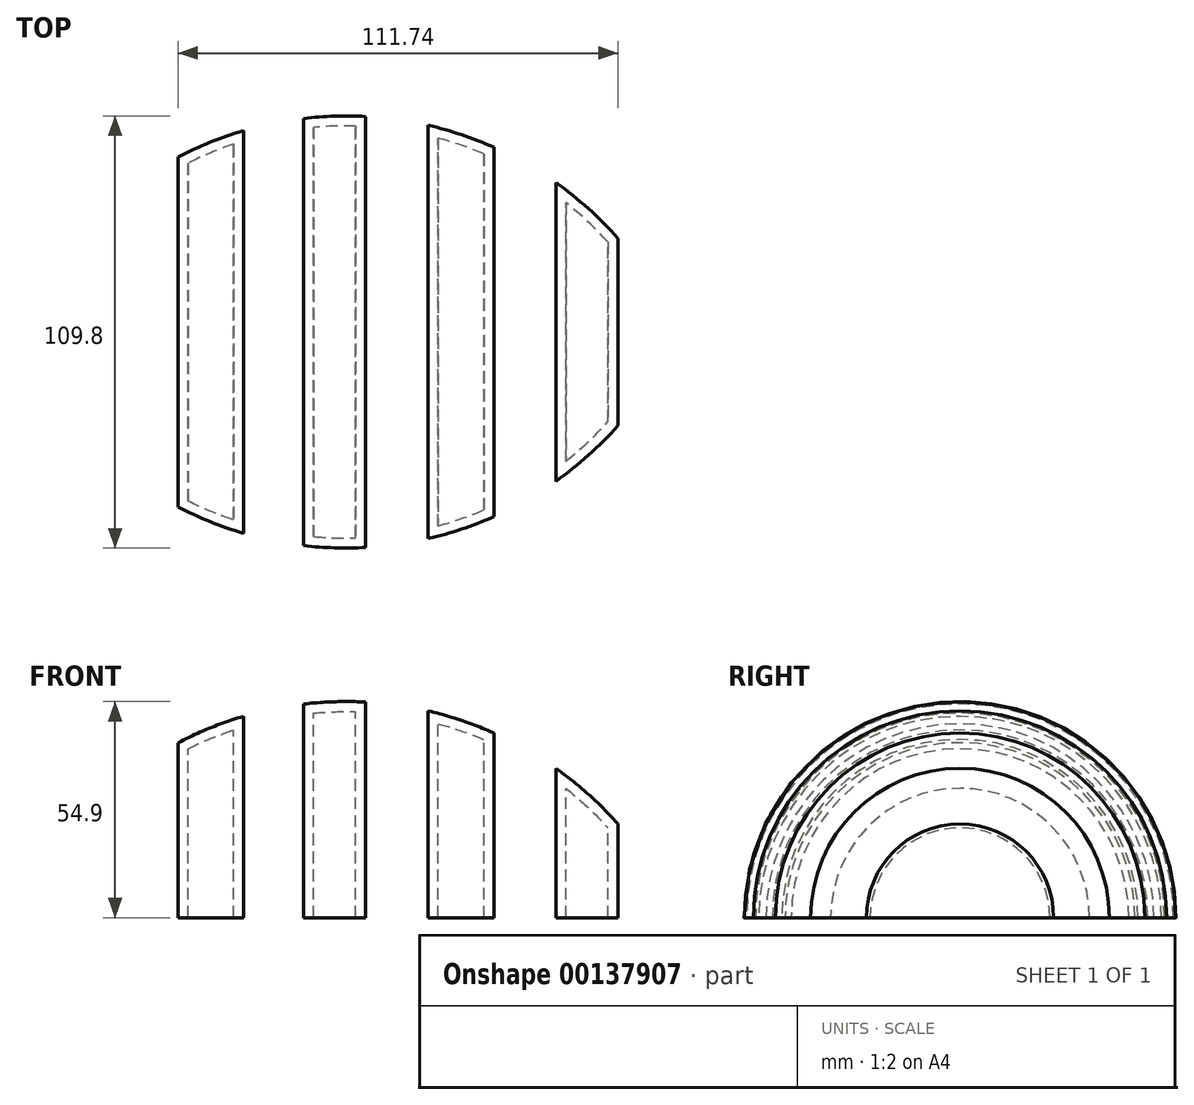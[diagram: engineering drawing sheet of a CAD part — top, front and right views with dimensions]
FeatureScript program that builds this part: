
annotation { "Feature Type Name" : "Feature", "Feature Type Description" : "" }
export const myFeature = defineFeature(function(context is Context, id is Id, definition is map)
    precondition{}
    {
        {
            var Q0;
            Q0=qCreatedBy(makeId("Front.planeOp"),FACE);
            var sketch = newSketch(context, id + "F0", { "sketchPlane" : qUnion([Q0])});
            skLineSegment(sketch, "E0", {"start": v(-53.58, -15.98) * mm, "end": v(-53.58, 28.47) * mm});
            skArc(sketch, "E1", {"start": v(58.16, 7.8) * mm, "mid": v(50.68, 15.33) * mm, "end": v(42.38, 21.95) * mm});
            skLineSegment(sketch, "E2", {"start": v(-53.58, -15.98) * mm, "end": v(-36.96, -15.98) * mm});
            skLineSegment(sketch, "E3", {"start": v(-36.96, -15.98) * mm, "end": v(-36.96, 35.17) * mm});
            skLineSegment(sketch, "E4", {"start": v(-21.69, -15.98) * mm, "end": v(-21.69, 38.29) * mm});
            skLineSegment(sketch, "E5", {"start": v(-5.91, -15.98) * mm, "end": v(-5.91, 38.78) * mm});
            skLineSegment(sketch, "E6", {"start": v(9.92, -15.98) * mm, "end": v(9.92, 36.53) * mm});
            skLineSegment(sketch, "E7", {"start": v(26.61, -15.98) * mm, "end": v(26.61, 30.93) * mm});
            skLineSegment(sketch, "E8", {"start": v(42.38, -15.98) * mm, "end": v(42.38, 21.95) * mm});
            skLineSegment(sketch, "E9", {"start": v(58.16, -15.98) * mm, "end": v(58.16, 7.8) * mm});
            skArc(sketch, "E10.trimOffspring", {"start": v(-36.96, 35.17) * mm, "mid": v(-45.43, 32.22) * mm, "end": v(-53.58, 28.47) * mm});
            skLineSegment(sketch, "E11.trimOffspring", {"start": v(-21.69, -15.98) * mm, "end": v(-5.91, -15.98) * mm});
            skArc(sketch, "E12.trimOffspring", {"start": v(-5.91, 38.78) * mm, "mid": v(-13.81, 38.87) * mm, "end": v(-21.69, 38.29) * mm});
            skLineSegment(sketch, "E13.trimOffspring", {"start": v(9.92, -15.98) * mm, "end": v(26.61, -15.98) * mm});
            skArc(sketch, "E14.trimOffspring", {"start": v(26.61, 30.93) * mm, "mid": v(18.4, 34.13) * mm, "end": v(9.92, 36.53) * mm});
            skLineSegment(sketch, "E15.trimOffspring", {"start": v(42.38, -15.98) * mm, "end": v(58.16, -15.98) * mm});
            skPoint(sketch, "E16.orphan", {"position": v(73.42, -15.98) * mm});
            skLineSegment(sketch, "E17", {"start": v(-53.58, -15.98) * mm, "end": v(58.16, -15.98) * mm});
            skSolve(sketch);
        }
        {
            var Q0;
            {var subQ0=sQuery(id+"F0.wireOp",EDGE,"E0");Q0=makeQuery(id+"F0.imprint","IMPRINT",FACE,{"disambiguationData":[TD([[makeQuery(id+"F0.imprint","IMPRINT",EDGE,{"derivedFrom":subQ0}),-1.0]])]});}
            var Q1;
            {var subQ0=sQuery(id+"F0.wireOp",EDGE,"E4");Q1=makeQuery(id+"F0.imprint","IMPRINT",FACE,{"disambiguationData":[TD([[makeQuery(id+"F0.imprint","IMPRINT",EDGE,{"derivedFrom":subQ0}),-1.0]])]});}
            var Q2;
            {var subQ0=sQuery(id+"F0.wireOp",EDGE,"E6");Q2=makeQuery(id+"F0.imprint","IMPRINT",FACE,{"disambiguationData":[TD([[makeQuery(id+"F0.imprint","IMPRINT",EDGE,{"derivedFrom":subQ0}),-1.0]])]});}
            var Q3;
            Q3=makeQuery(id+"F0.imprint","IMPRINT",FACE,{"disambiguationData":[TD([[makeQuery(id+"F0.imprint","IMPRINT",EDGE,{"derivedFrom":sQuery(id+"F0.wireOp",EDGE,"E1")}),1.0]])]});
            var Q4;
            Q4=sQuery(id+"F0.wireOp",EDGE,"E17");
            revolve(context, id + "F1", {"entities" : qUnion([Q0, Q1, Q2, Q3]), "axis" : qUnion([Q4]), "revolveType" : RevolveType.SYMMETRIC, "angle" : 180 * degree});
        }
        {
            var Q0;
            Q0=makeQuery(id+"F1.opRevolve","CAP_FACE",FACE,{"disambiguationData":[OSD([sQuery(id+"F0.wireOp",EDGE,"E0"),sQuery(id+"F0.wireOp",EDGE,"E3"),sQuery(id+"F0.wireOp",EDGE,"E10.trimOffspring"),sQuery(id+"F0.wireOp",EDGE,"E17")])],"isStart":false});
            var Q1;
            Q1=makeQuery(id+"F1.opRevolve","CAP_FACE",FACE,{"disambiguationData":[OSD([sQuery(id+"F0.wireOp",EDGE,"E4"),sQuery(id+"F0.wireOp",EDGE,"E5"),sQuery(id+"F0.wireOp",EDGE,"E12.trimOffspring"),sQuery(id+"F0.wireOp",EDGE,"E17")])],"isStart":false});
            var Q2;
            Q2=makeQuery(id+"F1.opRevolve","CAP_FACE",FACE,{"disambiguationData":[OSD([sQuery(id+"F0.wireOp",EDGE,"E6"),sQuery(id+"F0.wireOp",EDGE,"E7"),sQuery(id+"F0.wireOp",EDGE,"E14.trimOffspring"),sQuery(id+"F0.wireOp",EDGE,"E17")])],"isStart":false});
            var Q3;
            Q3=makeQuery(id+"F1.opRevolve","CAP_FACE",FACE,{"disambiguationData":[OSD([sQuery(id+"F0.wireOp",EDGE,"E1"),sQuery(id+"F0.wireOp",EDGE,"E8"),sQuery(id+"F0.wireOp",EDGE,"E9"),sQuery(id+"F0.wireOp",EDGE,"E17")])],"isStart":false});
            shell(context, id + "F2", {"entities" : qUnion([Q0, Q1, Q2, Q3]), "thickness" : 2.54 * mm});
        }
    });
